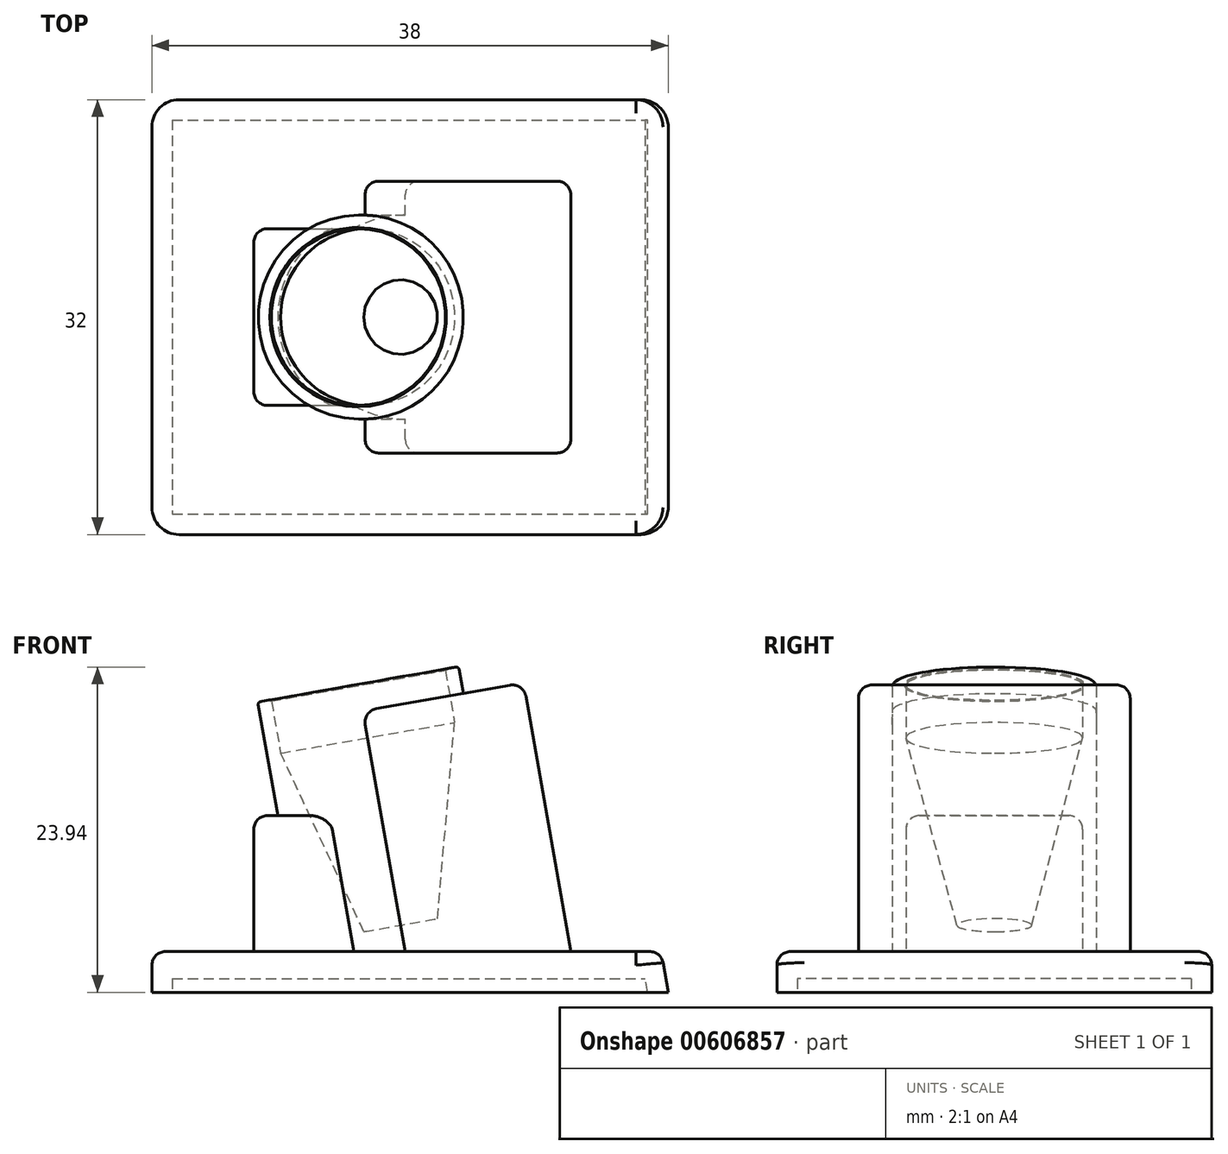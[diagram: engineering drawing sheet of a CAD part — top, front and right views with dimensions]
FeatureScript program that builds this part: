
annotation { "Feature Type Name" : "Feature", "Feature Type Description" : "" }
export const myFeature = defineFeature(function(context is Context, id is Id, definition is map)
    precondition{}
    {
        {
            var Q0;
            Q0=qCreatedBy(makeId("Front.planeOp"),FACE);
            var sketch = newSketch(context, id + "F0", { "sketchPlane" : qUnion([Q0])});
            skLineSegment(sketch, "E0.bottom", {"start": v(-19, 0) * mm, "end": v(19, 0) * mm});
            skLineSegment(sketch, "E0.top", {"start": v(-19, 3) * mm, "end": v(18.47, 3) * mm});
            skLineSegment(sketch, "E0.left", {"start": v(-19, 0) * mm, "end": v(-19, 3) * mm});
            skLineSegment(sketch, "E1", {"start": v(19, 0) * mm, "end": v(18.47, 3) * mm});
            skSolve(sketch);
        }
        {
            var Q0;
            Q0 = qSketchRegion(id + "F0", true);
            extrude(context, id + "F1", {"entities" : qUnion([Q0]), "endBound" : BoundingType.SYMMETRIC, "depth" : 32 * mm, "offsetDistance" : 25 * mm});
        }
        {
            var Q0;
            Q0=qCreatedBy(makeId("Front.planeOp"),FACE);
            var sketch = newSketch(context, id + "F2", { "sketchPlane" : qUnion([Q0])});
            skLineSegment(sketch, "E2", {"start": v(0, 1) * mm, "end": v(-3.82, 22.67) * mm, "construction": true});
            skLineSegment(sketch, "E3", {"start": v(-3.82, 22.67) * mm, "end": v(-11.2, 21.36) * mm, "construction": true});
            skLineSegment(sketch, "E4", {"start": v(-11.2, 21.36) * mm, "end": v(-7.39, -0.3) * mm, "construction": true});
            skLineSegment(sketch, "E5", {"start": v(0, 1) * mm, "end": v(-7.39, -0.3) * mm, "construction": true});
            skLineSegment(sketch, "E6", {"start": v(-11.2, 21.36) * mm, "end": v(-7.39, -0.3) * mm});
            skLineSegment(sketch, "E7", {"start": v(0, 1) * mm, "end": v(-7.39, -0.3) * mm});
            skLineSegment(sketch, "E8", {"start": v(-10.22, 21.54) * mm, "end": v(-9.53, 17.6) * mm, "construction": true});
            skLineSegment(sketch, "E9", {"start": v(-9.53, 17.6) * mm, "end": v(-3.4, 4.46) * mm, "construction": true});
            skLineSegment(sketch, "E10", {"start": v(-3.4, 4.46) * mm, "end": v(-0.7, 4.94) * mm, "construction": true});
            skLineSegment(sketch, "E11", {"start": v(-11.2, 21.36) * mm, "end": v(-3.82, 22.67) * mm});
            skLineSegment(sketch, "E12", {"start": v(-3.82, 22.67) * mm, "end": v(0, 1) * mm});
            skSolve(sketch);
        }
        {
            var Q0;
            Q0=makeQuery(id+"F2.imprint","IMPRINT",FACE,{"disambiguationData":[TD([[makeQuery(id+"F2.imprint","IMPRINT",EDGE,{"derivedFrom":sQuery(id+"F2.wireOp",EDGE,"E6")}),1.0]])]});
            var Q1;
            Q1=sQuery(id+"F2.wireOp",EDGE,"E2");
            revolve(context, id + "F3", {"operationType" : NewBodyOperationType.ADD, "entities" : qUnion([Q0]), "axis" : qUnion([Q1]), "revolveType" : RevolveType.FULL});
        }
        {
            var Q0;
            Q0=qCreatedBy(makeId("Front.planeOp"),FACE);
            var sketch = newSketch(context, id + "F4", { "sketchPlane" : qUnion([Q0])});
            skLineSegment(sketch, "E13.bottom", {"start": v(-17.5, 1) * mm, "end": v(17.3, 1) * mm});
            skLineSegment(sketch, "E13.top", {"start": v(-17.5, -3) * mm, "end": v(18, -3) * mm});
            skLineSegment(sketch, "E13.left", {"start": v(-17.5, 1) * mm, "end": v(-17.5, -3) * mm});
            skLineSegment(sketch, "E14", {"start": v(18, -3) * mm, "end": v(17.3, 1) * mm});
            skSolve(sketch);
        }
        {
            var Q0;
            Q0 = qSketchRegion(id + "F4", true);
            extrude(context, id + "F5", {"entities" : qUnion([Q0]), "operationType" : NewBodyOperationType.REMOVE, "endBound" : BoundingType.SYMMETRIC, "oppositeDirection" : true, "depth" : 29 * mm, "offsetDistance" : 25 * mm});
        }
        {
            var Q0;
            Q0=qCreatedBy(makeId("Front.planeOp"),FACE);
            var sketch = newSketch(context, id + "F6", { "sketchPlane" : qUnion([Q0])});
            skLineSegment(sketch, "E15", {"start": v(-3.47, 20.7) * mm, "end": v(8.34, 22.78) * mm});
            skLineSegment(sketch, "E16", {"start": v(8.34, 22.78) * mm, "end": v(11.83, 3) * mm});
            skLineSegment(sketch, "E17", {"start": v(11.83, 3) * mm, "end": v(-0.35, 3) * mm});
            skLineSegment(sketch, "E18", {"start": v(-0.35, 3) * mm, "end": v(-3.47, 20.7) * mm});
            skSolve(sketch);
        }
        {
            var Q0;
            Q0 = qSketchRegion(id + "F6", true);
            extrude(context, id + "F7", {"entities" : qUnion([Q0]), "operationType" : NewBodyOperationType.ADD, "endBound" : BoundingType.SYMMETRIC, "depth" : 20 * mm, "offsetDistance" : 25 * mm});
        }
        {
            var Q0;
            Q0=qCreatedBy(makeId("Front.planeOp"),FACE);
            var sketch = newSketch(context, id + "F8", { "sketchPlane" : qUnion([Q0])});
            skLineSegment(sketch, "E19.bottom", {"start": v(-11.5, 3) * mm, "end": v(0, 3) * mm});
            skLineSegment(sketch, "E19.top", {"start": v(-11.5, 13) * mm, "end": v(0, 13) * mm});
            skLineSegment(sketch, "E19.left", {"start": v(-11.5, 3) * mm, "end": v(-11.5, 13) * mm});
            skLineSegment(sketch, "E19.right", {"start": v(0, 3) * mm, "end": v(0, 13) * mm});
            skSolve(sketch);
        }
        {
            var Q0;
            Q0 = qSketchRegion(id + "F8", true);
            extrude(context, id + "F9", {"entities" : qUnion([Q0]), "operationType" : NewBodyOperationType.ADD, "endBound" : BoundingType.SYMMETRIC, "depth" : 13 * mm, "offsetDistance" : 25 * mm});
        }
        {
            var Q0;
            Q0=qCreatedBy(makeId("Front.planeOp"),FACE);
            var sketch = newSketch(context, id + "F10", { "sketchPlane" : qUnion([Q0])});
            skLineSegment(sketch, "E20.0", {"start": v(-10.2, 21.44) * mm, "end": v(-9.53, 17.6) * mm});
            skLineSegment(sketch, "E21.0", {"start": v(-9.53, 17.6) * mm, "end": v(-3.4, 4.46) * mm});
            skLineSegment(sketch, "E22.0", {"start": v(-3.4, 4.46) * mm, "end": v(-0.7, 4.94) * mm});
            skLineSegment(sketch, "E23.0", {"start": v(-3.82, 22.67) * mm, "end": v(-0.7, 4.94) * mm});
            skPoint(sketch, "E24.orphan", {"position": v(-11.2, 21.36) * mm});
            skPoint(sketch, "E25.orphan", {"position": v(0, 1) * mm});
            skLineSegment(sketch, "E26", {"start": v(-10.2, 21.44) * mm, "end": v(-10.3, 21.42) * mm});
            skLineSegment(sketch, "E27", {"start": v(-10.3, 21.42) * mm, "end": v(-10.32, 21.52) * mm});
            skPoint(sketch, "E28.0.end.orphan", {"position": v(-3.82, 22.67) * mm});
            skPoint(sketch, "E28.0.start.orphan", {"position": v(-10.22, 21.54) * mm});
            skLineSegment(sketch, "E29", {"start": v(-10.32, 21.52) * mm, "end": v(-3.82, 22.67) * mm});
            skSolve(sketch);
        }
        {
            var Q0;
            Q0 = qSketchRegion(id + "F10", true);
            var Q1;
            Q1=sQuery(id+"F2.wireOp",EDGE,"E12");
            revolve(context, id + "F11", {"operationType" : NewBodyOperationType.REMOVE, "entities" : qUnion([Q0]), "axis" : qUnion([Q1]), "revolveType" : RevolveType.FULL, "oppositeDirection" : true});
        }
        {
            var Q0;
            Q0=makeQuery(id+"F3.opRevolve","SWEPT_EDGE",EDGE,{"disambiguationData":[OSD([sQuery(id+"F2.wireOp",EDGE,"E6"),sQuery(id+"F2.wireOp",EDGE,"E11")])]});
            fillet(context, id + "F12", {"entities" : qUnion([Q0]), "radius" : .2 * mm, "tangentPropagation" : true, "allowEdgeOverflow" : false});
        }
        {
            var Q0;
            Q0=makeQuery(id+"F1.opExtrude","CAP_EDGE",EDGE,{"disambiguationData":[OSD([sQuery(id+"F0.wireOp",EDGE,"E0.left")])],"isStart":false});
            var Q1;
            Q1=makeQuery(id+"F1.opExtrude","CAP_EDGE",EDGE,{"disambiguationData":[OSD([sQuery(id+"F0.wireOp",EDGE,"E1")])],"isStart":false});
            var Q2;
            Q2=makeQuery(id+"F1.opExtrude","CAP_EDGE",EDGE,{"disambiguationData":[OSD([sQuery(id+"F0.wireOp",EDGE,"E0.left")])],"isStart":true});
            var Q3;
            Q3=makeQuery(id+"F1.opExtrude","CAP_EDGE",EDGE,{"disambiguationData":[OSD([sQuery(id+"F0.wireOp",EDGE,"E1")])],"isStart":true});
            fillet(context, id + "F13", {"entities" : qUnion([Q0, Q1, Q2, Q3]), "radius" : 2 * mm, "tangentPropagation" : true, "allowEdgeOverflow" : false});
        }
        {
            var Q0;
            Q0=makeQuery(id+"F1.opExtrude","CAP_EDGE",EDGE,{"disambiguationData":[OSD([sQuery(id+"F0.wireOp",EDGE,"E0.top")])],"isStart":true});
            fillet(context, id + "F14", {"entities" : qUnion([Q0]), "radius" : 1 * mm, "tangentPropagation" : true, "allowEdgeOverflow" : false});
        }
        {
            var Q0;
            Q0=makeQuery(id+"F9.opExtrude","CAP_EDGE",EDGE,{"disambiguationData":[OSD([sQuery(id+"F8.wireOp",EDGE,"E19.left")])],"isStart":true});
            var Q1;
            Q1=makeQuery(id+"F9.opExtrude","SWEPT_EDGE",EDGE,{"disambiguationData":[OSD([sQuery(id+"F8.wireOp",EDGE,"E19.top"),sQuery(id+"F8.wireOp",EDGE,"E19.left")])]});
            var Q2;
            Q2=makeQuery(id+"F9.opExtrude","CAP_EDGE",EDGE,{"disambiguationData":[OSD([sQuery(id+"F8.wireOp",EDGE,"E19.top")])],"isStart":true});
            var Q3;
            Q3=makeQuery(id+"F9.opExtrude","CAP_EDGE",EDGE,{"disambiguationData":[OSD([sQuery(id+"F8.wireOp",EDGE,"E19.top")])],"isStart":false});
            var Q4;
            Q4=makeQuery(id+"F9.opExtrude","CAP_EDGE",EDGE,{"disambiguationData":[OSD([sQuery(id+"F8.wireOp",EDGE,"E19.left")])],"isStart":false});
            fillet(context, id + "F15", {"entities" : qUnion([Q0, Q1, Q2, Q3, Q4]), "radius" : 1 * mm, "tangentPropagation" : true, "allowEdgeOverflow" : false});
        }
        {
            var Q0;
            Q0=makeQuery(id+"F7.opExtrude","CAP_EDGE",EDGE,{"disambiguationData":[OSD([sQuery(id+"F6.wireOp",EDGE,"E18")])],"isStart":true});
            var Q1;
            Q1=makeQuery(id+"F7.opExtrude","CAP_EDGE",EDGE,{"disambiguationData":[OSD([sQuery(id+"F6.wireOp",EDGE,"E16")])],"isStart":true});
            var Q2;
            Q2=makeQuery(id+"F7.opExtrude","CAP_EDGE",EDGE,{"disambiguationData":[OSD([sQuery(id+"F6.wireOp",EDGE,"E18")])],"isStart":false});
            var Q3;
            Q3=makeQuery(id+"F7.opExtrude","CAP_EDGE",EDGE,{"disambiguationData":[OSD([sQuery(id+"F6.wireOp",EDGE,"E16")])],"isStart":false});
            fillet(context, id + "F16", {"entities" : qUnion([Q0, Q1, Q2, Q3]), "radius" : 1 * mm, "tangentPropagation" : true, "allowEdgeOverflow" : false});
        }
        {
            var Q0;
            {var subQ0=sQuery(id+"F6.wireOp",EDGE,"E15");var subQ1=sQuery(id+"F6.wireOp",EDGE,"E18");Q0=makeQuery(id+"F7.boolean.opBoolean","SPLIT",EDGE,{"disambiguationData":[TD([makeQuery(id+"F7.opExtrude","CAP_FACE",FACE,{"disambiguationData":[OSD([subQ0,sQuery(id+"F6.wireOp",EDGE,"E16"),sQuery(id+"F6.wireOp",EDGE,"E17"),subQ1])],"isStart":true})])],"derivedFrom":makeQuery(id+"F7.opExtrude","SWEPT_EDGE",EDGE,{"disambiguationData":[OSD([subQ0,subQ1])]})});}
            fillet(context, id + "F17", {"entities" : qUnion([Q0]), "radius" : 1 * mm, "tangentPropagation" : true, "allowEdgeOverflow" : false});
        }
    });
